# Revit family: Drinking_Fountain-Haws_Corporation-Wall_Mounted_1011 new
name_source: partatom
category: Plumbing Fixtures
revit_build: Autodesk Revit Architecture 2015 (Build: 20160512_1515(x64)
units: mm (PartAtom-declared; Revit-internal decimal feet)

## types (6) — shared parameters
Amperage = 5 A
Apparent Load = 582 VA
Assembly Code = D2010810
Bowl Diameter = 1' - 2 1/8"
Cost Note = For Cost information please visit the Resource tab in the Product Page URL
Default Elevation = 2' - 3"
Flow = 0 GPM
HW Connection = No
Keynote = 15410.A1
Manufacturer = Haws Corporation
MasterFormat 2004 = 22 47 00,22 47 13,22 52 00,22 52 13
Number of Poles = 1
OmniClass 23 = 23-65 70 14,23-65 70 14 11,23-65 70 14 11 11
Power Consumption = 575 VA
Power Factor = 0.987745
Product Documentation Link = https://www.hawsco.com
Product Name = The Haws 1011 barrier free Hi-Lo drinking fountain
Product Page URL = http://www.hawsco.com
Revisions Date = 05/24/2009
Sanitary Radius = 0' - 0 5/8"
Series = The Haws 1011 barrier free Hi-Lo drinking fountain
Supply Radius = 0' - 0 3/16"
Tubing = Metal - Haws Corporation - Copper
URL = http://www.hawsco.com
Vent Connection = Yes
Version = 2014-v2.0a
Voltage = 115 V
Waste Level = 2' - 4 3/32"
zero-valued in all types: Cost

## per-type parameters (varying)
| type | Back Plate | Bowl | Bracket | CW Connection | CWFU | Description | Grille | HWFU | Left Syphon pos. | Lo Knob | Right Syphone pos. | Sensor Eye | Trim | Trim Plate | Trim Plate Short | Tubing pos.R | Type Comments | Void Height | WFU | Waste Connection | con L |
| 1011 | Metal - Haws Corporation - Satin Stainless Steel | Metal - Haws Corporation - Satin Stainless Steel | Metal - Haws Corporation - Satin Stainless Steel | No | 1 | "Hi-Lo" design allows for twice the users as regular fountains and suits the needs for various user heights. | No | 0 | 0.00° | Yes | 0.00° | No | Metal - Haws Corporation - Satin Stainless Steel | No | No | 0' - 1 41/128" | Placed securely in multiple locations without taking up excess space | 1' - 4 3/4" | 1 | No | Yes |
| 1011HPS | Metal - Haws Corporation - High Polished Stainless Steel | Metal - Haws Corporation - High Polished Stainless Steel | Metal - Haws Corporation - High Polished Stainless Steel | No | 1 | Barrier-free "Hi-Lo" drinking fountain uses a patented push-button valve assembly | No | 0 | 0.00° | Yes | 0.00° | No | Metal - Haws Corporation - High Polished Stainless Steel | No | No | 0' - 1 41/128" | High-polished stainless steel finish, and matching back panel | 1' - 4 3/4" | 1 | No | Yes |
| 1011HPSMS | Metal - Haws Corporation - High Polished Stainless Steel | Metal - Haws Corporation - High Polished Stainless Steel | Metal - Haws Corporation - High Polished Stainless Steel | Yes | 3 | Barrier-free "Hi-Lo" drinking fountain uses a patented push-button valve assembly | No | 0 | 180.00° | Yes | 0.00° | No | Metal - Haws Corporation - High Polished Stainless Steel | No | Yes | 0' - 1 41/128" | Design with a high-polished stainless steel finish and front access of plumbing | 2' - 1 3/4" | 2 | Yes | Yes |
| 1011MS | Metal - Haws Corporation - Satin Stainless Steel | Metal - Haws Corporation - Satin Stainless Steel | Metal - Haws Corporation - Satin Stainless Steel | Yes | 3 | Barrier free "Hi-Lo" drinking fountain uses a patented push-button valve assembly | No | 0 | 180.00° | Yes | 0.00° | No | Metal - Haws Corporation - Satin Stainless Steel | No | Yes | 0' - 1 41/128" | MS (mounting system) allows for front access of P-trap and stop. | 2' - 1 3/4" | 2 | Yes | Yes |
| H1011.8HO | Metal - Haws Corporation - Satin Stainless Steel | Metal - Haws Corporation - Satin Stainless Steel | Metal - Haws Corporation - Satin Stainless Steel | Yes | 2 | (Hands off) "Hi-Lo" electric drinking fountain provides 8 gph chilled water performance | Yes | 1 | 90.00° | No | 90.00° | Yes | Metal - Haws Corporation - Satin Stainless Steel | Yes | No | 0' - 3 241/256" | "Hands off" feature allows the lower fountain to be activated without the use of the operator’s hands, better protecting it from germs and assisting in the ease of use to the handicap. | 3' - 3 1/4" | 3 | No | No |
| H1011.8HPS | Metal - Haws Corporation - High Polished Stainless Steel | Metal - Haws Corporation - High Polished Stainless Steel | Metal - Haws Corporation - High Polished Stainless Steel | Yes | 2 | "Hi-Lo" electric drinking fountain provides 8 gph chilled water performance | Yes | 0 | 90.00° | Yes | 90.00° | No | Metal - Haws Corporation - High Polished Stainless Steel | Yes | No | 0' - 3 241/256" | Design with back panel  in an engineered polished stainless steel skin | 3' - 3 1/4" | 3 | No | No |

note: column(s) folded — value = type name in every type: Model

## geometry (parser evidence)
native form markers: Blend x24, Sweep x13
no freeform markers — native parametric forms only
